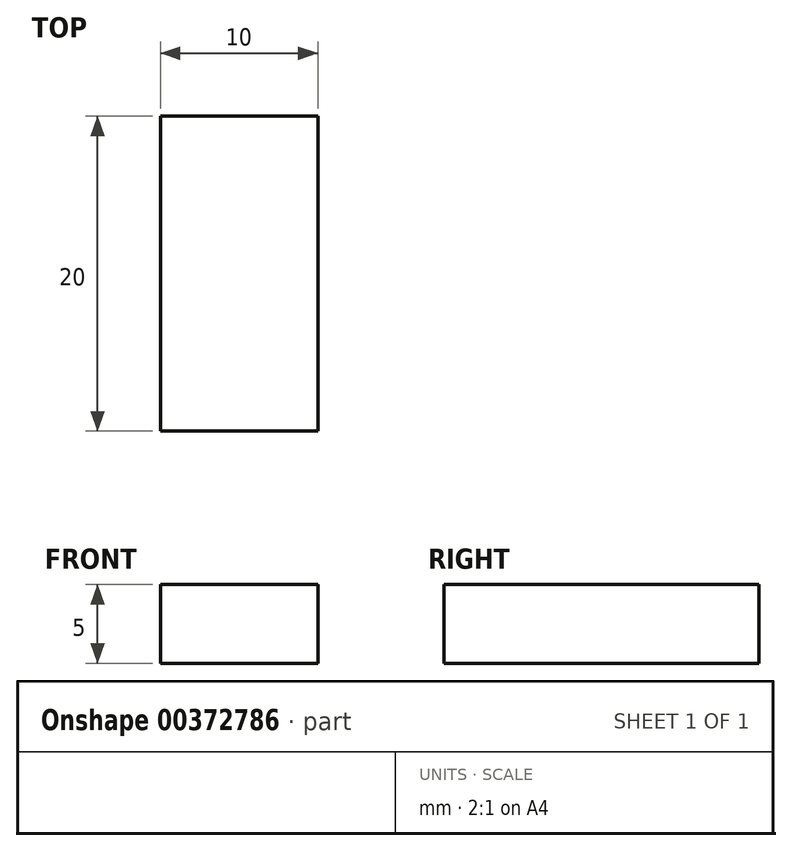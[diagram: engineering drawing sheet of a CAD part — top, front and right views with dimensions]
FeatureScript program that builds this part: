
annotation { "Feature Type Name" : "Feature", "Feature Type Description" : "" }
export const myFeature = defineFeature(function(context is Context, id is Id, definition is map)
    precondition{}
    {
        {
            var Q0;
            Q0=qCreatedBy(makeId("Front.planeOp"),FACE);
            var sketch = newSketch(context, id + "F0", { "sketchPlane" : qUnion([Q0])});
            skLineSegment(sketch, "E0.bottom", {"start": v(0, -0.67) * mm, "end": v(10, -0.67) * mm});
            skLineSegment(sketch, "E0.top", {"start": v(0, 4.33) * mm, "end": v(10, 4.33) * mm});
            skLineSegment(sketch, "E0.left", {"start": v(0, -0.67) * mm, "end": v(0, 4.33) * mm});
            skLineSegment(sketch, "E0.right", {"start": v(10, -0.67) * mm, "end": v(10, 4.33) * mm});
            skSolve(sketch);
        }
        {
            var Q0;
            Q0 = qSketchRegion(id + "F0", true);
            extrude(context, id + "F1", {"entities" : qUnion([Q0]), "depth" : 20 * mm});
        }
    });
